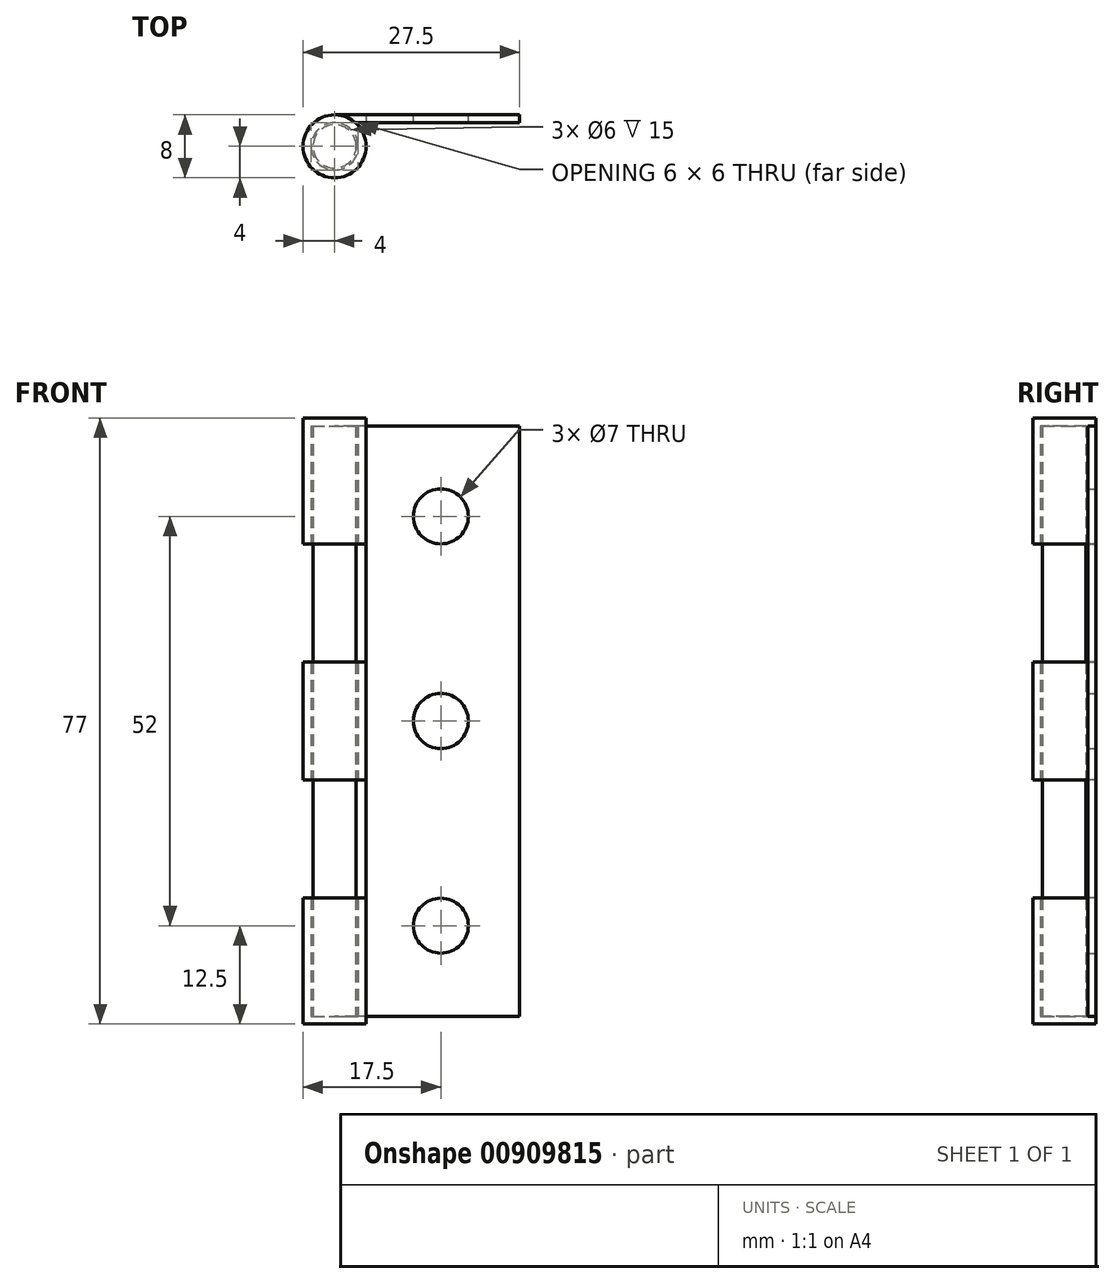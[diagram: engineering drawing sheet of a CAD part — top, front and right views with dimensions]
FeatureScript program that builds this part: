
annotation { "Feature Type Name" : "Feature", "Feature Type Description" : "" }
export const myFeature = defineFeature(function(context is Context, id is Id, definition is map)
    precondition{}
    {
        {
            var Q0;
            Q0=qCreatedBy(makeId("Front.planeOp"),FACE);
            var sketch = newSketch(context, id + "F0", { "sketchPlane" : qUnion([Q0])});
            skLineSegment(sketch, "E0.bottom", {"start": v(0, 37.5) * mm, "end": v(-20, 37.5) * mm});
            skLineSegment(sketch, "E0.top", {"start": v(0, -37.5) * mm, "end": v(-20, -37.5) * mm});
            skLineSegment(sketch, "E0.left", {"start": v(0, 37.5) * mm, "end": v(0, -37.5) * mm});
            skLineSegment(sketch, "E0.right", {"start": v(-20, 37.5) * mm, "end": v(-20, -37.5) * mm});
            skCircle(sketch, "E1", {"center": v(-10, 26) * mm, "radius": 3.5 * mm});
            skCircle(sketch, "E2", {"center": v(-10, 0) * mm, "radius": 3.5 * mm});
            skCircle(sketch, "E3", {"center": v(-10, -26) * mm, "radius": 3.5 * mm});
            skSolve(sketch);
        }
        {
            var Q0;
            Q0=makeQuery(id+"F0.imprint","IMPRINT",FACE,{"disambiguationData":[TD([[makeQuery(id+"F0.imprint","IMPRINT",EDGE,{"derivedFrom":sQuery(id+"F0.wireOp",EDGE,"E0.bottom")}),1.0]])]});
            extrude(context, id + "F1", {"entities" : qUnion([Q0]), "depth" : 1 * mm, "offsetDistance" : 25 * mm});
        }
        {
            var Q0;
            Q0=makeQuery(id+"F1.opExtrude","SWEPT_FACE",FACE,{"disambiguationData":[OSD([sQuery(id+"F0.wireOp",EDGE,"E0.top")])]});
            var sketch = newSketch(context, id + "F2", { "sketchPlane" : qUnion([Q0])});
            skCircle(sketch, "E4", {"center": v(-23.5, 4) * mm, "radius": 4 * mm});
            skLineSegment(sketch, "E5", {"start": v(-20, 0) * mm, "end": v(-23.5, 0) * mm});
            skLineSegment(sketch, "E6", {"start": v(-20, 1) * mm, "end": v(-20.85, 1) * mm});
            skCircle(sketch, "E7", {"center": v(-23.5, 4) * mm, "radius": 3 * mm});
            skSolve(sketch);
        }
        {
            var Q0;
            Q0 = qSketchRegion(id + "F2", true);
            var Q1;
            {var subQ0=sQuery(id+"F2.wireOp",EDGE,"E5");Q1=makeQuery(id+"F2.imprint","IMPRINT",FACE,{"disambiguationData":[TD([[makeQuery(id+"F2.imprint","IMPRINT",EDGE,{"derivedFrom":subQ0}),-1.0]])]});}
            var Q2;
            Q2=makeQuery(id+"F1.opExtrude","SWEPT_FACE",FACE,{"disambiguationData":[OSD([sQuery(id+"F0.wireOp",EDGE,"E0.bottom")])]});
            extrude(context, id + "F3", {"entities" : qUnion([Q0, Q1]), "operationType" : NewBodyOperationType.ADD, "endBound" : BoundingType.UP_TO_SURFACE, "oppositeDirection" : true, "depth" : 25 * mm, "endBoundEntityFace" : qUnion([Q2]), "offsetDistance" : 25 * mm});
        }
        {
            var Q0;
            Q0=makeQuery(id+"F3.boolean.opBoolean","MERGE",FACE,{"derivedFrom":[makeQuery(id+"F1.opExtrude","CAP_FACE",FACE,{"disambiguationData":[OSD([sQuery(id+"F0.wireOp",EDGE,"E0.bottom"),sQuery(id+"F0.wireOp",EDGE,"E0.top"),sQuery(id+"F0.wireOp",EDGE,"E0.left"),sQuery(id+"F0.wireOp",EDGE,"E0.right"),sQuery(id+"F0.wireOp",EDGE,"E1"),sQuery(id+"F0.wireOp",EDGE,"E2"),sQuery(id+"F0.wireOp",EDGE,"E3")])],"isStart":false}),makeQuery(id+"F3.opExtrude","SWEPT_FACE",FACE,{"disambiguationData":[OSD([sQuery(id+"F2.wireOp",EDGE,"E6")])]})]});
            var sketch = newSketch(context, id + "F4", { "sketchPlane" : qUnion([Q0])});
            skLineSegment(sketch, "E8.bottom", {"start": v(-19.5, -7.5) * mm, "end": v(-27.5, -7.5) * mm});
            skLineSegment(sketch, "E8.top", {"start": v(-19.5, -22.5) * mm, "end": v(-27.5, -22.5) * mm});
            skLineSegment(sketch, "E8.left", {"start": v(-19.5, -7.5) * mm, "end": v(-19.5, -22.5) * mm});
            skLineSegment(sketch, "E8.right", {"start": v(-27.5, -7.5) * mm, "end": v(-27.5, -22.5) * mm});
            skLineSegment(sketch, "E9.bottom", {"start": v(-27.5, 22.5) * mm, "end": v(-19.5, 22.5) * mm});
            skLineSegment(sketch, "E9.top", {"start": v(-27.5, 7.5) * mm, "end": v(-19.5, 7.5) * mm});
            skLineSegment(sketch, "E9.left", {"start": v(-27.5, 22.5) * mm, "end": v(-27.5, 7.5) * mm});
            skLineSegment(sketch, "E9.right", {"start": v(-19.5, 22.5) * mm, "end": v(-19.5, 7.5) * mm});
            skPoint(sketch, "E10.startSnap0", {"position": v(-19.5, 15) * mm});
            skSolve(sketch);
        }
        {
            var Q0;
            Q0 = qSketchRegion(id + "F4", true);
            extrude(context, id + "F5", {"entities" : qUnion([Q0]), "operationType" : NewBodyOperationType.REMOVE, "endBound" : BoundingType.THROUGH_ALL, "oppositeDirection" : true, "depth" : 25 * mm, "offsetDistance" : 25 * mm, "hasSecondDirection" : true, "secondDirectionBound" : SecondDirectionBoundingType.THROUGH_ALL, "secondDirectionOppositeDirection" : false, "secondDirectionDepth" : 25 * mm});
        }
        {
            var Q0;
            {var subQ0=sQuery(id+"F0.wireOp",EDGE,"E0.top");Q0=makeQuery(id+"F3.boolean.opBoolean","MERGE",FACE,{"derivedFrom":[makeQuery(id+"F1.opExtrude","SWEPT_FACE",FACE,{"disambiguationData":[OSD([subQ0])]}),makeQuery(id+"F3.opExtrude","CAP_FACE",FACE,{"disambiguationData":[OSD([subQ0,sQuery(id+"F0.wireOp",EDGE,"E0.right"),sQuery(id+"F2.wireOp",EDGE,"E4"),sQuery(id+"F2.wireOp",EDGE,"E5"),sQuery(id+"F2.wireOp",EDGE,"E6"),sQuery(id+"F2.wireOp",EDGE,"E7")])],"isStart":true})]});}
            var sketch = newSketch(context, id + "F6", { "sketchPlane" : qUnion([Q0])});
            skCircle(sketch, "E11", {"center": v(-23.5, 4) * mm, "radius": 2.75 * mm});
            skSolve(sketch);
        }
        {
            var Q0;
            Q0 = qSketchRegion(id + "F6", true);
            var Q1;
            Q1=makeQuery(id+"F3.boolean.opBoolean","MERGE",FACE,{"derivedFrom":[makeQuery(id+"F1.opExtrude","SWEPT_FACE",FACE,{"disambiguationData":[OSD([sQuery(id+"F0.wireOp",EDGE,"E0.bottom")])]}),makeQuery(id+"F3.opExtrude","CAP_FACE",FACE,{"disambiguationData":[OSD([sQuery(id+"F0.wireOp",EDGE,"E0.top"),sQuery(id+"F0.wireOp",EDGE,"E0.right"),sQuery(id+"F2.wireOp",EDGE,"E4"),sQuery(id+"F2.wireOp",EDGE,"E5"),sQuery(id+"F2.wireOp",EDGE,"E6"),sQuery(id+"F2.wireOp",EDGE,"E7")])],"isStart":false})]});
            extrude(context, id + "F7", {"entities" : qUnion([Q0]), "endBound" : BoundingType.UP_TO_SURFACE, "oppositeDirection" : true, "depth" : 25 * mm, "endBoundEntityFace" : qUnion([Q1]), "offsetDistance" : 25 * mm});
        }
        {
            var Q0;
            Q0=makeQuery(id+"F7.opExtrude","CAP_FACE",FACE,{"disambiguationData":[OSD([sQuery(id+"F6.wireOp",EDGE,"E11")])],"isStart":false});
            var sketch = newSketch(context, id + "F8", { "sketchPlane" : qUnion([Q0])});
            skCircle(sketch, "E12", {"center": v(-23.5, -4) * mm, "radius": 4 * mm});
            skSolve(sketch);
        }
        {
            var Q0;
            Q0 = qSketchRegion(id + "F8", true);
            extrude(context, id + "F9", {"entities" : qUnion([Q0]), "operationType" : NewBodyOperationType.ADD, "depth" : 1 * mm, "offsetDistance" : 25 * mm});
        }
        {
            var Q0;
            Q0=makeQuery(id+"F7.opExtrude","CAP_FACE",FACE,{"disambiguationData":[OSD([sQuery(id+"F6.wireOp",EDGE,"E11")])],"isStart":true});
            var sketch = newSketch(context, id + "F10", { "sketchPlane" : qUnion([Q0])});
            skCircle(sketch, "E13", {"center": v(-23.5, 4) * mm, "radius": 4 * mm});
            skSolve(sketch);
        }
        {
            var Q0;
            Q0 = qSketchRegion(id + "F10", true);
            extrude(context, id + "F11", {"entities" : qUnion([Q0]), "operationType" : NewBodyOperationType.ADD, "depth" : 1 * mm, "offsetDistance" : 25 * mm});
        }
    });
